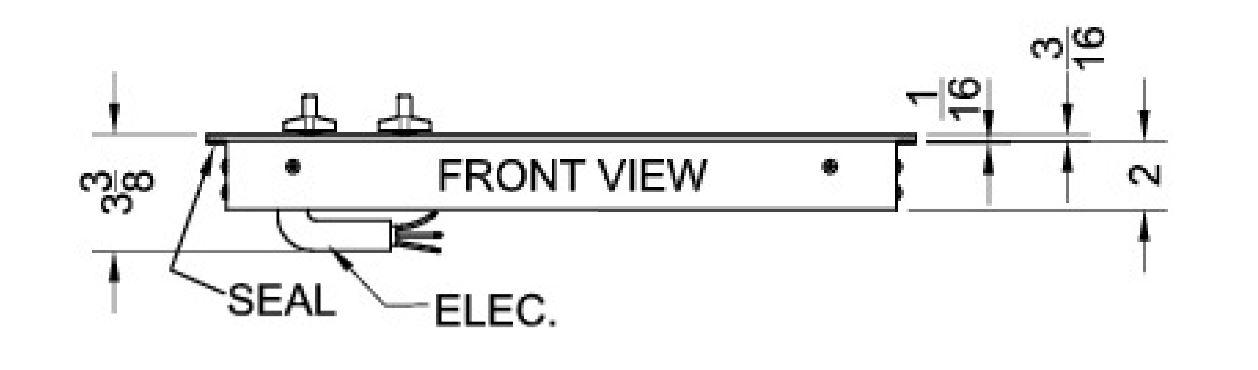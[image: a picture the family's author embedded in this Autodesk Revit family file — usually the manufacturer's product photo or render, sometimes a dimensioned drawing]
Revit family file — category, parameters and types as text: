
# Revit family: QF_Summit_CR3240_Electric Cooktop
name_source: partatom
category: Specialty Equipment
units: mm (PartAtom-declared; Revit-internal decimal feet)

## family parameters
Always vertical = Yes
Cut with Voids When Loaded = No
Part Type = Normal
Room Calculation Point = No
Round Connector Dimension = Use Diameter
Shared = No
Work Plane-Based = No

## types (1)
- QF_Summit_CR3240_Electric Cooktop
    Apparent Power = 9200 VA
    Conn Conduit = Yes
    Cycle = 60 Hz
    Default Elevation = 0"
    Depth = 19 1/8"
    Description = Electric Cooktop
    Elec Conn Connection Height = 0"
    Elec Conn RI Height = 0"
    FL Amps = 40 A
    Foodservice Equipment Identifier = Yes
    Height = 3 3/8"
    Identify Quantity as Lot = Yes
    Length = 20 5/8"
    Manufacturer = Summit
    Max Overcurrent Protection = 0 A
    Min Ckt Ampacity = 0 A
    Model = CR3240
    Number of Poles = 1
    Phase = 1
    Volts = 230 V
    Watts = 9200 W
    Weight in Pounds = 15

## geometry (parser evidence)
native form markers: Sweep x2
no freeform markers — native parametric forms only
